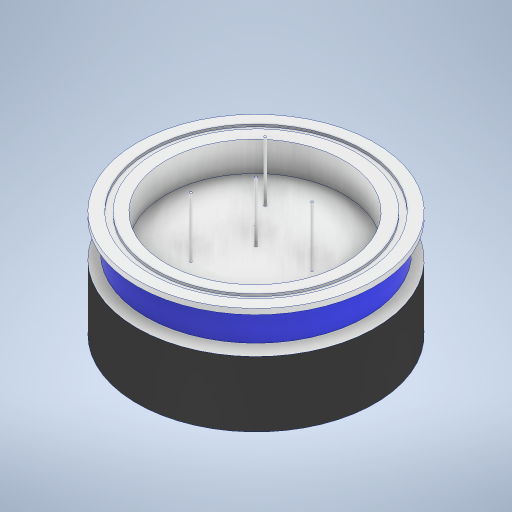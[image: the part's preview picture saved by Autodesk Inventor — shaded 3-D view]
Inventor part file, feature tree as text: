
AUTODESK INVENTOR PART (.ipt)
format: ipt  version: 2024 (Build 280153000, 153)  size: 332,288 bytes
history: native  units: mm
features: extrude x5, sketch x4, revolve x1
ambient origin geometry x8: Origin, YZ Plane, XZ Plane, XY Plane, X Axis, Y Axis, Z Axis, Center Point
bodies: Solid1 (feature_tree)
feature tree (10):
  sketch  "Sketch1"  dims[d0=200.0mm d1=180.0mm]
  extrude  "Extrusion1"  Depth=180.0mm
  extrude  "Extrusion2"  Depth=8.0mm TaperAngle=0.0deg
  extrude  "Extrusion3"  Depth=80.0mm TaperAngle=0.0deg
  extrude  "Extrusion4"  Depth=25.0mm TaperAngle=0.0deg
  revolve  "Revolution1"  Angle=120.0deg
  extrude  "Extrusion7"  TaperAngle=60.0deg  [1 undecoded]
  sketch  "Sketch2"  dims[d2=170.0mm d3=8.0mm d4=0.0mm]
  sketch  "Sketch3"  dims[d5=10.0mm d6=0.0mm d7=80.0mm d8=0.0mm]
  sketch  "Sketch6"  dims[d9=150.0mm d10=25.0mm d11=0.0mm d12=120.0deg d13=60.0deg d14=90.0deg d32=84.0mm d33=2.0mm d34=30.0mm d36=360.0deg d38=50.0mm d39=0.0mm d40=2.0mm]
note: 1 required parameter value undecoded (feature->parameter linkage not recoverable at this tier; creation-order binding heuristic only, values carry confidence <= 0.55)
